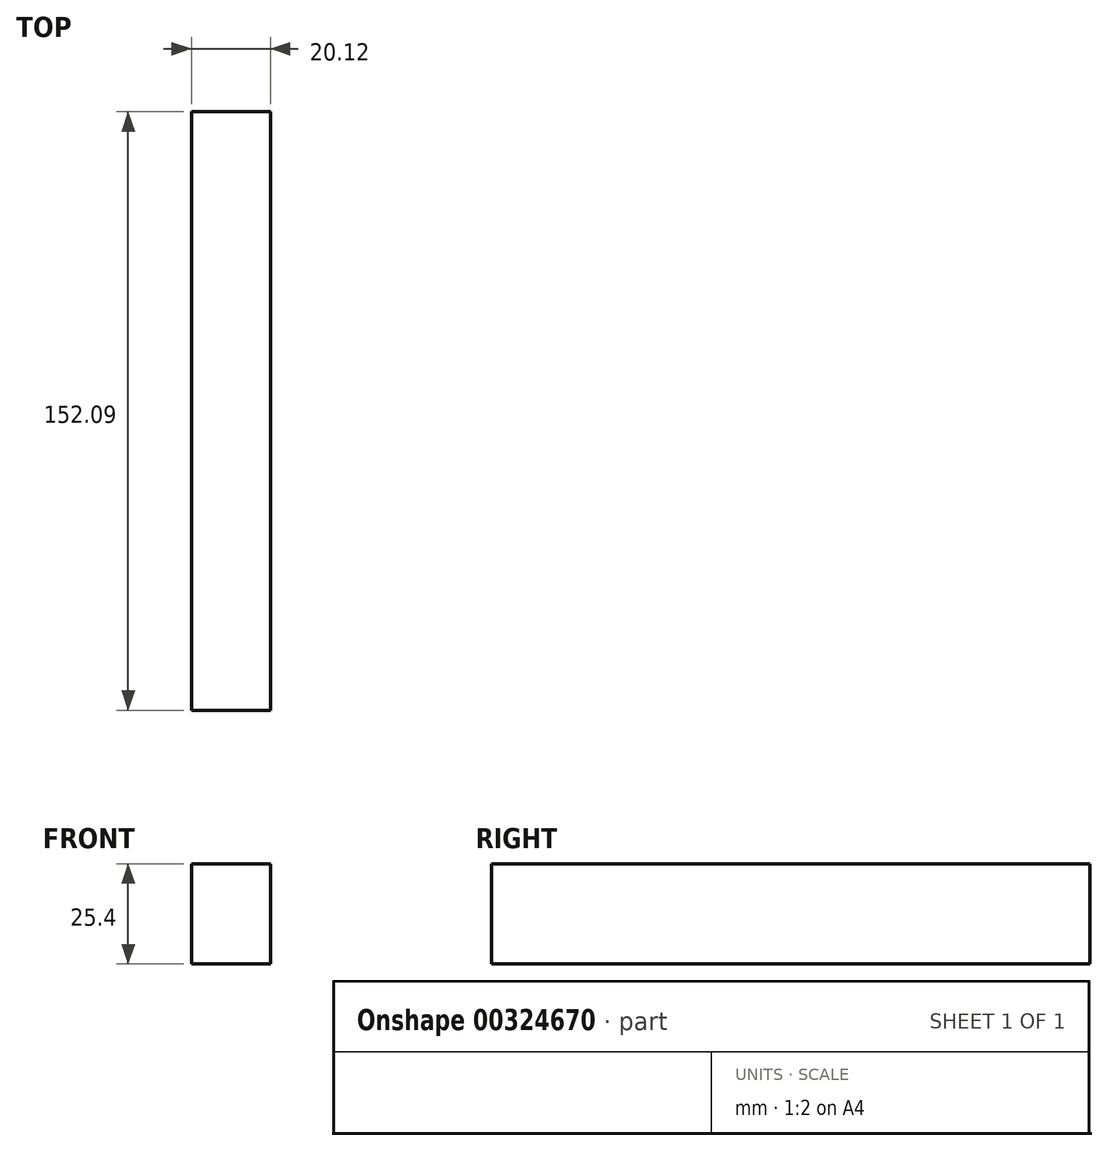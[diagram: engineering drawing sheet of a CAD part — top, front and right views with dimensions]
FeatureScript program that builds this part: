
annotation { "Feature Type Name" : "Feature", "Feature Type Description" : "" }
export const myFeature = defineFeature(function(context is Context, id is Id, definition is map)
    precondition{}
    {
        {
            var Q0;
            Q0=qCreatedBy(makeId("Top.planeOp"),FACE);
            var sketch = newSketch(context, id + "F0", { "sketchPlane" : qUnion([Q0])});
            skLineSegment(sketch, "E0.bottom", {"start": v(-76.2, 75.74) * mm, "end": v(-56.08, 75.74) * mm});
            skLineSegment(sketch, "E0.top", {"start": v(-76.2, -76.35) * mm, "end": v(-56.08, -76.35) * mm});
            skLineSegment(sketch, "E0.left", {"start": v(-76.2, 75.74) * mm, "end": v(-76.2, -76.35) * mm});
            skLineSegment(sketch, "E0.right", {"start": v(-56.08, 75.74) * mm, "end": v(-56.08, -76.35) * mm});
            skSolve(sketch);
        }
        {
            var Q0;
            Q0 = qSketchRegion(id + "F0", true);
            extrude(context, id + "F1", {"entities" : qUnion([Q0]), "depth" : 25.4 * mm});
        }
    });
